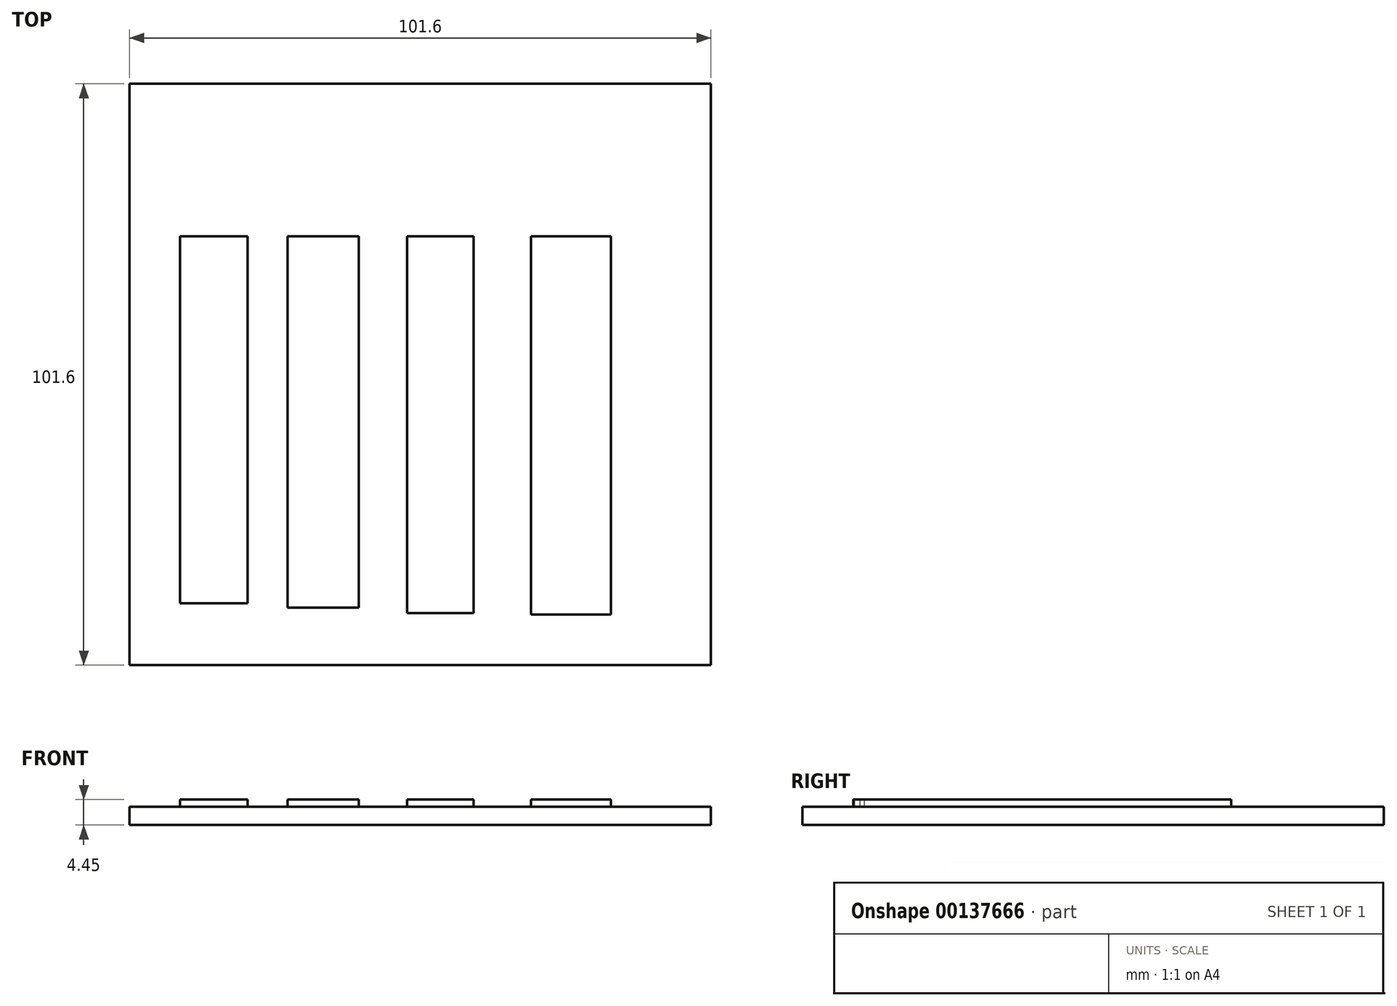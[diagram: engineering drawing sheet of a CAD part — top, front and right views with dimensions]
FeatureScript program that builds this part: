
annotation { "Feature Type Name" : "Feature", "Feature Type Description" : "" }
export const myFeature = defineFeature(function(context is Context, id is Id, definition is map)
    precondition{}
    {
        {
            var Q0;
            Q0=qCreatedBy(makeId("Top.planeOp"),FACE);
            var sketch = newSketch(context, id + "F0", { "sketchPlane" : qUnion([Q0])});
            skLineSegment(sketch, "E0.bottom", {"start": v(-35.26, 26.67) * mm, "end": v(66.34, 26.67) * mm});
            skLineSegment(sketch, "E0.top", {"start": v(-35.26, -74.93) * mm, "end": v(66.34, -74.93) * mm});
            skLineSegment(sketch, "E0.left", {"start": v(-35.26, 26.67) * mm, "end": v(-35.26, -74.93) * mm});
            skLineSegment(sketch, "E0.right", {"start": v(66.34, 26.67) * mm, "end": v(66.34, -74.93) * mm});
            skSolve(sketch);
        }
        {
            var Q0;
            Q0=makeQuery(id+"F0.imprint","IMPRINT",FACE,{"disambiguationData":[TD([[makeQuery(id+"F0.imprint","IMPRINT",EDGE,{"derivedFrom":sQuery(id+"F0.wireOp",EDGE,"E0.bottom")}),-1.0]])]});
            extrude(context, id + "F1", {"entities" : qUnion([Q0]), "depth" : 3.17 * mm});
        }
        {
            var Q0;
            Q0=makeQuery(id+"F1.opExtrude","CAP_FACE",FACE,{"disambiguationData":[OSD([sQuery(id+"F0.wireOp",EDGE,"E0.bottom"),sQuery(id+"F0.wireOp",EDGE,"E0.top"),sQuery(id+"F0.wireOp",EDGE,"E0.left"),sQuery(id+"F0.wireOp",EDGE,"E0.right")])],"isStart":false});
            var sketch = newSketch(context, id + "F2", { "sketchPlane" : qUnion([Q0])});
            skLineSegment(sketch, "E1.bottom", {"start": v(-26.43, 0) * mm, "end": v(-14.61, 0) * mm});
            skLineSegment(sketch, "E1.top", {"start": v(-26.43, -64.14) * mm, "end": v(-14.61, -64.14) * mm});
            skLineSegment(sketch, "E1.left", {"start": v(-26.43, 0) * mm, "end": v(-26.43, -64.14) * mm});
            skLineSegment(sketch, "E1.right", {"start": v(-14.61, 0) * mm, "end": v(-14.61, -64.14) * mm});
            skSolve(sketch);
        }
        {
            var Q0;
            Q0=makeQuery(id+"F2.imprint","IMPRINT",FACE,{"disambiguationData":[TD([[makeQuery(id+"F2.imprint","IMPRINT",EDGE,{"derivedFrom":sQuery(id+"F2.wireOp",EDGE,"E1.bottom")}),-1.0]])]});
            extrude(context, id + "F3", {"entities" : qUnion([Q0]), "operationType" : NewBodyOperationType.ADD, "depth" : 1.27 * mm});
        }
        {
            var Q0;
            Q0=makeQuery(id+"F1.opExtrude","CAP_FACE",FACE,{"disambiguationData":[OSD([sQuery(id+"F0.wireOp",EDGE,"E0.bottom"),sQuery(id+"F0.wireOp",EDGE,"E0.top"),sQuery(id+"F0.wireOp",EDGE,"E0.left"),sQuery(id+"F0.wireOp",EDGE,"E0.right")])],"isStart":false});
            var sketch = newSketch(context, id + "F4", { "sketchPlane" : qUnion([Q0])});
            skLineSegment(sketch, "E2.bottom", {"start": v(-7.68, 0) * mm, "end": v(4.8, 0) * mm});
            skLineSegment(sketch, "E2.top", {"start": v(-7.68, -64.91) * mm, "end": v(4.8, -64.91) * mm});
            skLineSegment(sketch, "E2.left", {"start": v(-7.68, 0) * mm, "end": v(-7.68, -64.91) * mm});
            skLineSegment(sketch, "E2.right", {"start": v(4.8, 0) * mm, "end": v(4.8, -64.91) * mm});
            skSolve(sketch);
        }
        {
            var Q0;
            Q0=makeQuery(id+"F4.imprint","IMPRINT",FACE,{"disambiguationData":[TD([[makeQuery(id+"F4.imprint","IMPRINT",EDGE,{"derivedFrom":sQuery(id+"F4.wireOp",EDGE,"E2.bottom")}),-1.0]])]});
            extrude(context, id + "F5", {"entities" : qUnion([Q0]), "operationType" : NewBodyOperationType.ADD, "depth" : 1.27 * mm});
        }
        {
            var Q0;
            Q0=makeQuery(id+"F1.opExtrude","CAP_FACE",FACE,{"disambiguationData":[OSD([sQuery(id+"F0.wireOp",EDGE,"E0.bottom"),sQuery(id+"F0.wireOp",EDGE,"E0.top"),sQuery(id+"F0.wireOp",EDGE,"E0.left"),sQuery(id+"F0.wireOp",EDGE,"E0.right")])],"isStart":false});
            var sketch = newSketch(context, id + "F6", { "sketchPlane" : qUnion([Q0])});
            skLineSegment(sketch, "E3.bottom", {"start": v(13.24, 0) * mm, "end": v(24.84, 0) * mm});
            skLineSegment(sketch, "E3.top", {"start": v(13.24, -65.85) * mm, "end": v(24.84, -65.85) * mm});
            skLineSegment(sketch, "E3.left", {"start": v(13.24, 0) * mm, "end": v(13.24, -65.85) * mm});
            skLineSegment(sketch, "E3.right", {"start": v(24.84, 0) * mm, "end": v(24.84, -65.85) * mm});
            skSolve(sketch);
        }
        {
            var Q0;
            Q0=makeQuery(id+"F6.imprint","IMPRINT",FACE,{"disambiguationData":[TD([[makeQuery(id+"F6.imprint","IMPRINT",EDGE,{"derivedFrom":sQuery(id+"F6.wireOp",EDGE,"E3.bottom")}),-1.0]])]});
            extrude(context, id + "F7", {"entities" : qUnion([Q0]), "operationType" : NewBodyOperationType.ADD, "depth" : 1.27 * mm});
        }
        {
            var Q0;
            Q0=makeQuery(id+"F1.opExtrude","CAP_FACE",FACE,{"disambiguationData":[OSD([sQuery(id+"F0.wireOp",EDGE,"E0.bottom"),sQuery(id+"F0.wireOp",EDGE,"E0.top"),sQuery(id+"F0.wireOp",EDGE,"E0.left"),sQuery(id+"F0.wireOp",EDGE,"E0.right")])],"isStart":false});
            var sketch = newSketch(context, id + "F8", { "sketchPlane" : qUnion([Q0])});
            skLineSegment(sketch, "E4.bottom", {"start": v(34.92, 0) * mm, "end": v(48.84, 0) * mm});
            skLineSegment(sketch, "E4.top", {"start": v(34.92, -66.08) * mm, "end": v(48.84, -66.08) * mm});
            skLineSegment(sketch, "E4.left", {"start": v(34.92, 0) * mm, "end": v(34.92, -66.08) * mm});
            skLineSegment(sketch, "E4.right", {"start": v(48.84, 0) * mm, "end": v(48.84, -66.08) * mm});
            skSolve(sketch);
        }
        {
            var Q0;
            Q0=makeQuery(id+"F8.imprint","IMPRINT",FACE,{"disambiguationData":[TD([[makeQuery(id+"F8.imprint","IMPRINT",EDGE,{"derivedFrom":sQuery(id+"F8.wireOp",EDGE,"E4.bottom")}),-1.0]])]});
            extrude(context, id + "F9", {"entities" : qUnion([Q0]), "operationType" : NewBodyOperationType.ADD, "depth" : 1.27 * mm});
        }
    });
